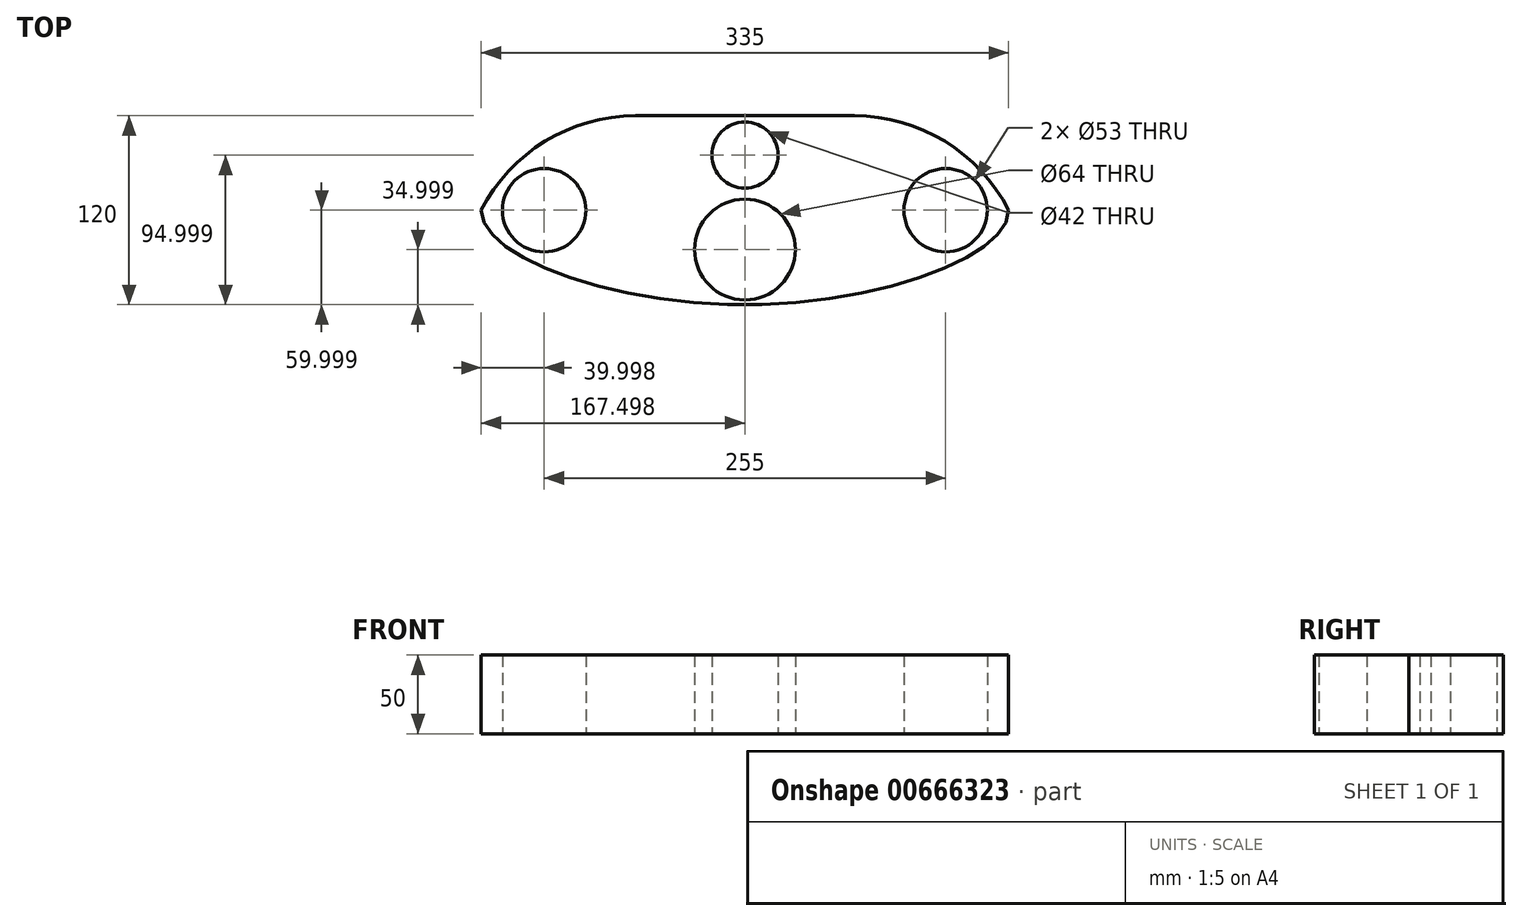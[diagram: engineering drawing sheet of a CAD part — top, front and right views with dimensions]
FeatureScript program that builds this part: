
annotation { "Feature Type Name" : "Feature", "Feature Type Description" : "" }
export const myFeature = defineFeature(function(context is Context, id is Id, definition is map)
    precondition{}
    {
        {
            var Q0;
            Q0=qCreatedBy(makeId("Top.planeOp"),FACE);
            var sketch = newSketch(context, id + "F0", { "sketchPlane" : qUnion([Q0])});
            skLineSegment(sketch, "E0.bottom", {"start": v(-165.78, 16.17) * mm, "end": v(169.22, 16.17) * mm});
            skLineSegment(sketch, "E0.top", {"start": v(-165.78, 136.17) * mm, "end": v(169.22, 136.17) * mm});
            skLineSegment(sketch, "E0.left", {"start": v(-165.78, 16.17) * mm, "end": v(-165.78, 136.17) * mm});
            skLineSegment(sketch, "E0.right", {"start": v(169.22, 16.17) * mm, "end": v(169.22, 136.17) * mm});
            skPoint(sketch, "E1", {"position": v(1.72, 111.17) * mm});
            skPoint(sketch, "E1.positionSnap0", {"position": v(1.72, 136.17) * mm});
            skPoint(sketch, "E2", {"position": v(1.72, 51.17) * mm});
            skPoint(sketch, "E3", {"position": v(-125.78, 76.17) * mm});
            skPoint(sketch, "E3.positionSnap0", {"position": v(-165.78, 76.17) * mm});
            skPoint(sketch, "E4", {"position": v(129.22, 76.17) * mm});
            skPoint(sketch, "E4.positionSnap0", {"position": v(169.22, 76.17) * mm});
            skCircle(sketch, "E5", {"center": v(-125.78, 76.17) * mm, "radius": 26.5 * mm});
            skCircle(sketch, "E6", {"center": v(129.22, 76.17) * mm, "radius": 26.5 * mm});
            skCircle(sketch, "E7", {"center": v(1.72, 51.17) * mm, "radius": 32 * mm});
            skCircle(sketch, "E8", {"center": v(1.72, 111.17) * mm, "radius": 21 * mm});
            skSolve(sketch);
        }
        {
            var Q0;
            Q0=qSketchRegion(id+"F0",true);
            extrude(context, id + "F1", {"entities" : qUnion([Q0]), "depth" : 50 * mm, "offsetDistance" : 25 * mm});
        }
        {
            var Q0;
            Q0=makeQuery(id+"F1.opExtrude","CAP_FACE",FACE,{"disambiguationData":[OSD([sQuery(id+"F0.wireOp",EDGE,"E0.bottom"),sQuery(id+"F0.wireOp",EDGE,"E0.top"),sQuery(id+"F0.wireOp",EDGE,"E0.left"),sQuery(id+"F0.wireOp",EDGE,"E0.right"),sQuery(id+"F0.wireOp",EDGE,"E5"),sQuery(id+"F0.wireOp",EDGE,"E6"),sQuery(id+"F0.wireOp",EDGE,"E7"),sQuery(id+"F0.wireOp",EDGE,"E8")])],"isStart":false});
            var sketch = newSketch(context, id + "F2", { "sketchPlane" : qUnion([Q0])});
            skFitSpline(sketch, "E9", {"points": [v(1.72, 16.17) * mm, v(-165.78, 76.17) * mm, v(1.72, 136.17) * mm, v(169.22, 76.17) * mm, v(1.72, 16.17) * mm]});
            skSolve(sketch);
        }
        {
            var Q0;
            {var subQ0=sQuery(id+"F2.wireOp",EDGE,"E9");var subQ1=makeQuery(id+"F1.opExtrude","CAP_EDGE",EDGE,{"disambiguationData":[OSD([sQuery(id+"F0.wireOp",EDGE,"E0.left")])],"isStart":false});var subQ2=makeQuery(id+"F2.imprint","INTERSECT",VERTEX,{"derivedFrom":[subQ1,subQ0]});Q0=makeQuery(id+"F2.imprint","IMPRINT",FACE,{"disambiguationData":[TD([[makeQuery(id+"F2.imprint","IMPRINT",EDGE,{"disambiguationData":[TD([[subQ2,1.0]])],"derivedFrom":subQ0}),1.0]])]});}
            var Q1;
            {var subQ0=sQuery(id+"F2.wireOp",EDGE,"E9");var subQ1=makeQuery(id+"F1.opExtrude","CAP_EDGE",EDGE,{"disambiguationData":[OSD([sQuery(id+"F0.wireOp",EDGE,"E0.bottom")])],"isStart":false});var subQ2=makeQuery(id+"F2.imprint","INTERSECT",VERTEX,{"derivedFrom":[subQ1,subQ0]});Q1=makeQuery(id+"F2.imprint","IMPRINT",FACE,{"disambiguationData":[TD([[makeQuery(id+"F2.imprint","IMPRINT",EDGE,{"disambiguationData":[TD([[subQ2,1.0]])],"derivedFrom":subQ0}),1.0]])]});}
            extrude(context, id + "F3", {"entities" : qUnion([Q0, Q1]), "operationType" : NewBodyOperationType.REMOVE, "oppositeDirection" : true, "depth" : 60 * mm, "offsetDistance" : 25 * mm});
        }
        {
            var Q0;
            Q0=makeQuery(id+"F1.opExtrude","SWEPT_EDGE",EDGE,{"disambiguationData":[OSD([sQuery(id+"F0.wireOp",EDGE,"E0.top"),sQuery(id+"F0.wireOp",EDGE,"E0.right")])]});
            var Q1;
            Q1=makeQuery(id+"F1.opExtrude","SWEPT_EDGE",EDGE,{"disambiguationData":[OSD([sQuery(id+"F0.wireOp",EDGE,"E0.top"),sQuery(id+"F0.wireOp",EDGE,"E0.left")])]});
            fillet(context, id + "F4", {"entities" : qUnion([Q0, Q1]), "radius" : 110 * mm, "tangentPropagation" : true, "allowEdgeOverflow" : false});
        }
    });
